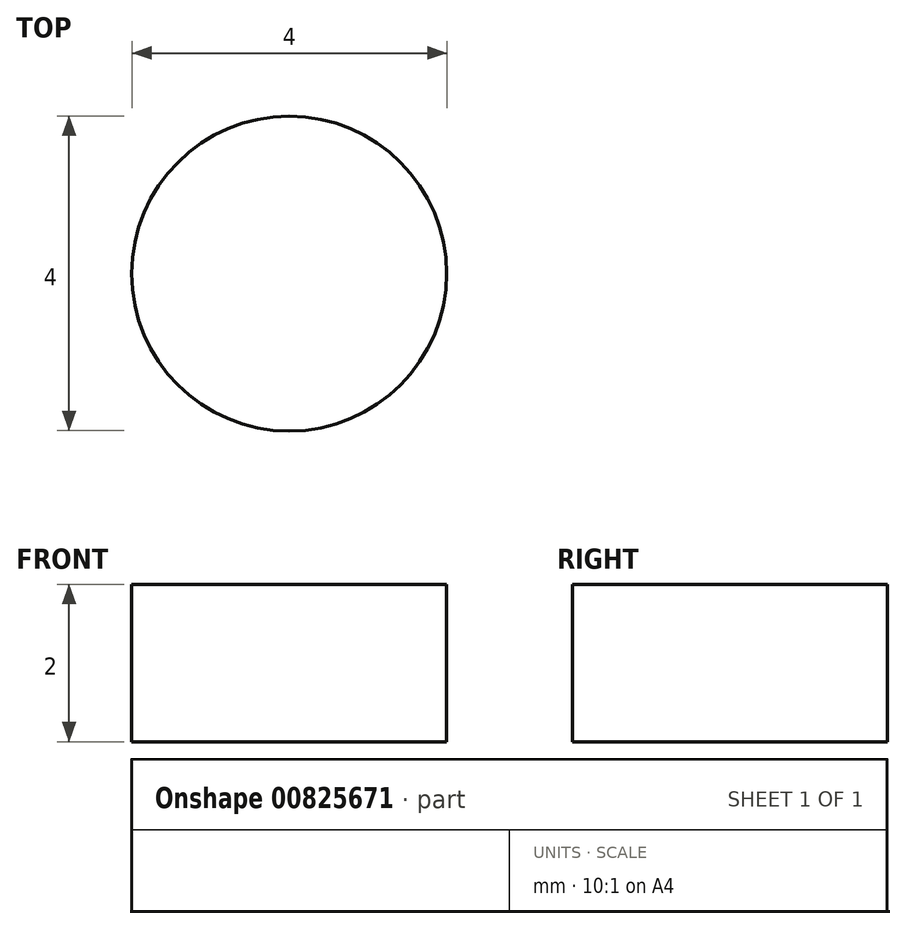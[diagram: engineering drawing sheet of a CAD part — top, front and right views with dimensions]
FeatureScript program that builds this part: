
annotation { "Feature Type Name" : "Feature", "Feature Type Description" : "" }
export const myFeature = defineFeature(function(context is Context, id is Id, definition is map)
    precondition{}
    {
        {
            var Q0;
            Q0=qCreatedBy(makeId("Top.planeOp"),FACE);
            var sketch = newSketch(context, id + "F0", { "sketchPlane" : qUnion([Q0])});
            skCircle(sketch, "E0", {"center": v(-18, -15.95) * mm, "radius": 2 * mm});
            skSolve(sketch);
        }
        {
            var Q0;
            Q0=makeQuery(id+"F0.imprint","IMPRINT",FACE,{"disambiguationData":[TD([[makeQuery(id+"F0.imprint","IMPRINT",EDGE,{"derivedFrom":sQuery(id+"F0.wireOp",EDGE,"E0")}),1.0]])]});
            extrude(context, id + "F1", {"entities" : qUnion([Q0]), "depth" : 2 * mm, "offsetDistance" : 25 * mm});
        }
    });
